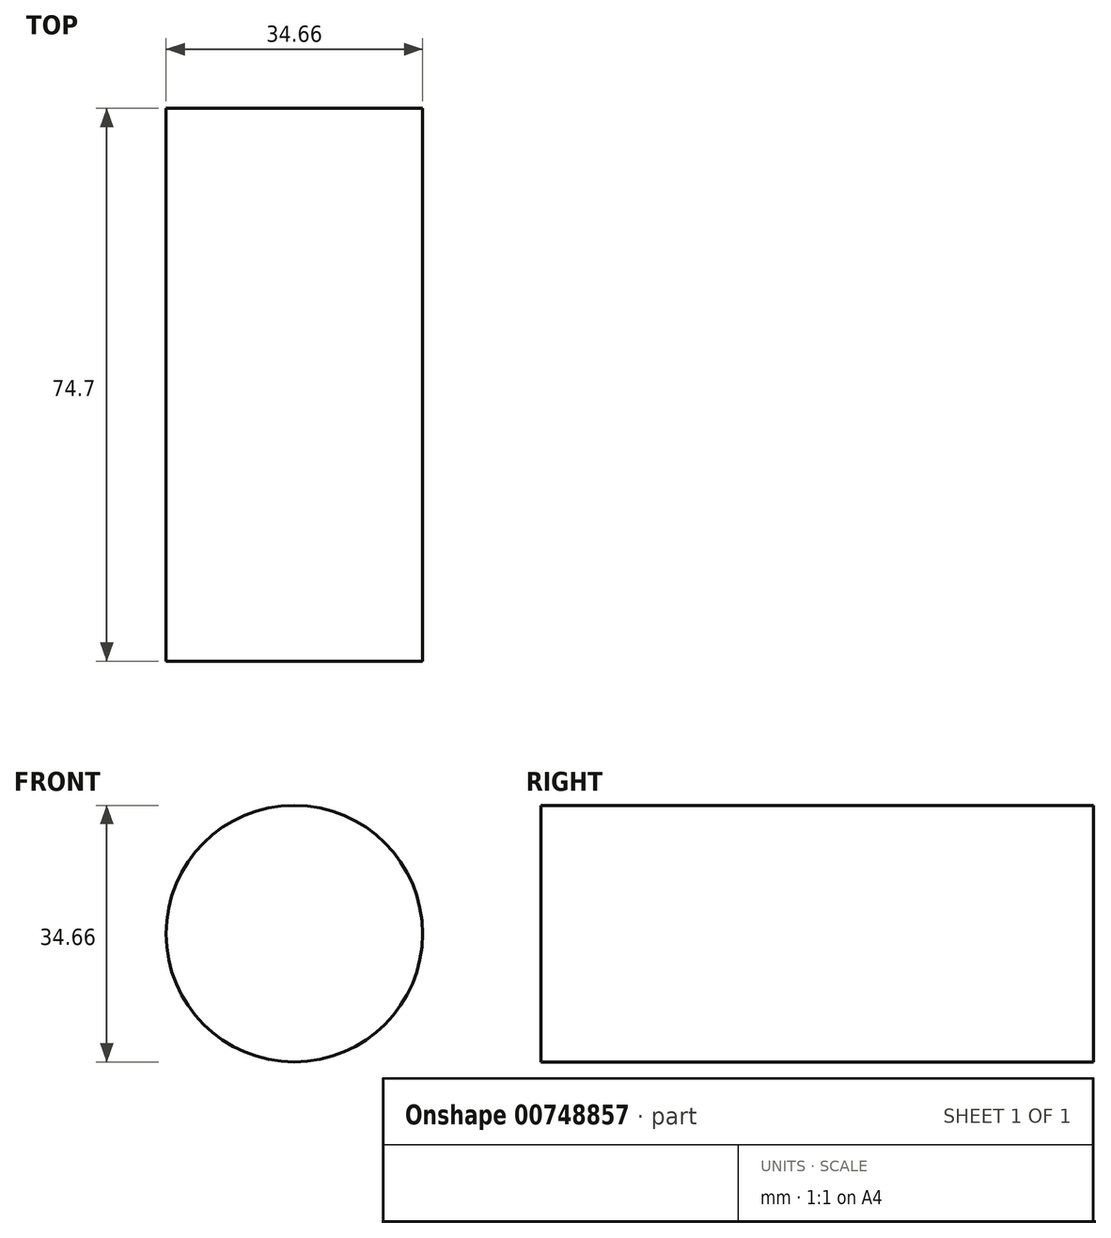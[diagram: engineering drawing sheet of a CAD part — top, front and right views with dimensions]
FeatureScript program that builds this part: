
annotation { "Feature Type Name" : "Feature", "Feature Type Description" : "" }
export const myFeature = defineFeature(function(context is Context, id is Id, definition is map)
    precondition{}
    {
        {
            var Q0;
            Q0=qCreatedBy(makeId("Front.planeOp"),FACE);
            var sketch = newSketch(context, id + "F0", { "sketchPlane" : qUnion([Q0])});
            skCircle(sketch, "E0", {"center": v(0, 0) * mm, "radius": 17.33 * mm});
            skSolve(sketch);
        }
        {
            var Q0;
            Q0 = qSketchRegion(id + "F0", true);
            extrude(context, id + "F1", {"entities" : qUnion([Q0]), "depth" : 74.7 * mm, "offsetDistance" : 25.4 * mm});
        }
    });
